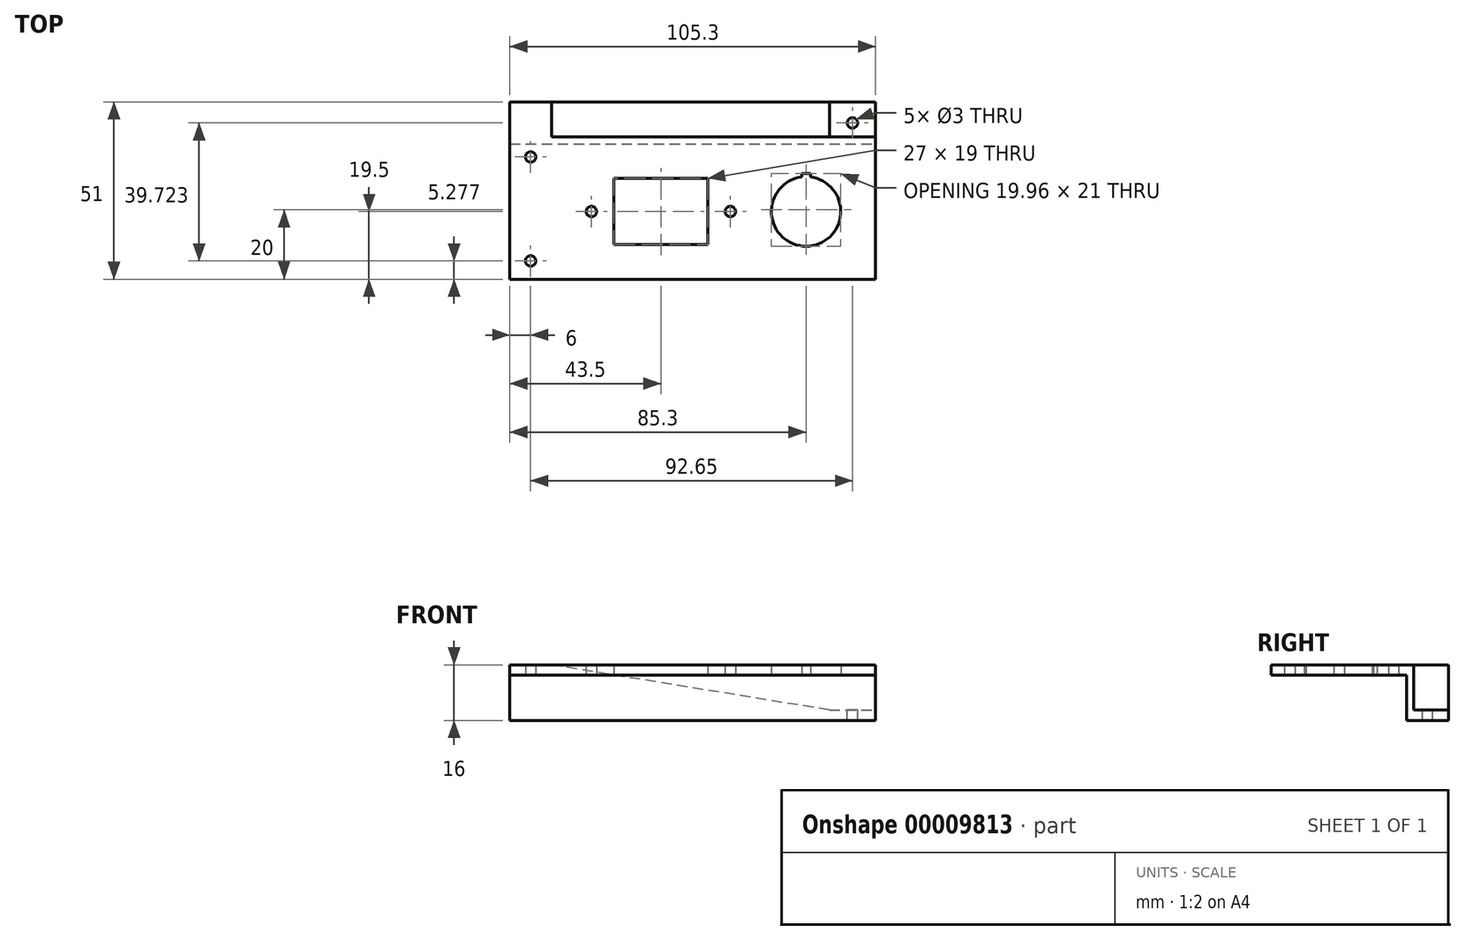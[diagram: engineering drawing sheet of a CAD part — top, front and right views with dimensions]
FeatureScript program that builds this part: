
annotation { "Feature Type Name" : "Feature", "Feature Type Description" : "" }
export const myFeature = defineFeature(function(context is Context, id is Id, definition is map)
    precondition{}
    {
        {
            var Q0;
            Q0=qCreatedBy(makeId("Top.planeOp"),FACE);
            var sketch = newSketch(context, id + "F0", { "sketchPlane" : qUnion([Q0])});
            skLineSegment(sketch, "E0.bottom", {"start": v(-13.5, 9.5) * mm, "end": v(13.5, 9.5) * mm});
            skLineSegment(sketch, "E0.top", {"start": v(-13.5, -9.5) * mm, "end": v(13.5, -9.5) * mm});
            skLineSegment(sketch, "E0.left", {"start": v(-13.5, 9.5) * mm, "end": v(-13.5, -9.5) * mm});
            skLineSegment(sketch, "E0.right", {"start": v(13.5, 9.5) * mm, "end": v(13.5, -9.5) * mm});
            skCircle(sketch, "E1", {"center": v(-20, 0) * mm, "radius": 1.5 * mm});
            skCircle(sketch, "E2.0.MirrorC", {"center": v(20, 0) * mm, "radius": 1.5 * mm});
            skCircle(sketch, "E3", {"center": v(41.8, 0) * mm, "radius": 10 * mm});
            skLineSegment(sketch, "E4", {"start": v(40.55, 9.92) * mm, "end": v(40.55, 11) * mm});
            skLineSegment(sketch, "E5", {"start": v(40.55, 11) * mm, "end": v(43.05, 11) * mm});
            skLineSegment(sketch, "E6", {"start": v(43.05, 11) * mm, "end": v(43.05, 9.92) * mm});
            skLineSegment(sketch, "E7.bottom", {"start": v(-43.5, 31.5) * mm, "end": v(61.8, 31.5) * mm});
            skLineSegment(sketch, "E7.top", {"start": v(-43.5, -19.5) * mm, "end": v(61.8, -19.5) * mm});
            skLineSegment(sketch, "E7.left", {"start": v(-43.5, 31.5) * mm, "end": v(-43.5, -19.5) * mm});
            skLineSegment(sketch, "E7.right", {"start": v(61.8, 31.5) * mm, "end": v(61.8, -19.5) * mm});
            skCircle(sketch, "E8", {"center": v(-37.5, -14.22) * mm, "radius": 1.5 * mm});
            skCircle(sketch, "E9", {"center": v(-37.5, 15.7) * mm, "radius": 1.5 * mm});
            skSolve(sketch);
        }
        {
            var Q0;
            Q0=makeQuery(id+"F0.imprint","IMPRINT",FACE,{"disambiguationData":[TD([[makeQuery(id+"F0.imprint","IMPRINT",EDGE,{"derivedFrom":sQuery(id+"F0.wireOp",EDGE,"E0.bottom")}),1.0]])]});
            extrude(context, id + "F1", {"entities" : qUnion([Q0]), "depth" : 3 * mm});
        }
        {
            var Q0;
            Q0=makeQuery(id+"F1.opExtrude","CAP_FACE",FACE,{"disambiguationData":[OSD([sQuery(id+"F0.wireOp",EDGE,"E0.bottom"),sQuery(id+"F0.wireOp",EDGE,"E0.top"),sQuery(id+"F0.wireOp",EDGE,"E0.left"),sQuery(id+"F0.wireOp",EDGE,"E0.right"),sQuery(id+"F0.wireOp",EDGE,"E1"),sQuery(id+"F0.wireOp",EDGE,"E2.0.MirrorC"),sQuery(id+"F0.wireOp",EDGE,"E3"),sQuery(id+"F0.wireOp",EDGE,"E4"),sQuery(id+"F0.wireOp",EDGE,"E5"),sQuery(id+"F0.wireOp",EDGE,"E6"),sQuery(id+"F0.wireOp",EDGE,"E7.bottom"),sQuery(id+"F0.wireOp",EDGE,"E7.top"),sQuery(id+"F0.wireOp",EDGE,"E7.left"),sQuery(id+"F0.wireOp",EDGE,"E7.right")])],"isStart":true});
            var sketch = newSketch(context, id + "F2", { "sketchPlane" : qUnion([Q0])});
            skLineSegment(sketch, "E10.bottom", {"start": v(-43.5, -31.5) * mm, "end": v(61.8, -31.5) * mm});
            skLineSegment(sketch, "E10.top", {"start": v(-43.5, -19.5) * mm, "end": v(61.8, -19.5) * mm});
            skLineSegment(sketch, "E10.left", {"start": v(-43.5, -31.5) * mm, "end": v(-43.5, -19.5) * mm});
            skLineSegment(sketch, "E10.right", {"start": v(61.8, -31.5) * mm, "end": v(61.8, -19.5) * mm});
            skSolve(sketch);
        }
        {
            var Q0;
            Q0=makeQuery(id+"F2.imprint","IMPRINT",FACE,{"disambiguationData":[TD([[makeQuery(id+"F2.imprint","IMPRINT",EDGE,{"derivedFrom":sQuery(id+"F2.wireOp",EDGE,"E10.bottom")}),1.0]])]});
            extrude(context, id + "F3", {"entities" : qUnion([Q0]), "operationType" : NewBodyOperationType.ADD, "depth" : 13 * mm});
        }
        {
            var Q0;
            Q0=makeQuery(id+"F1.opExtrude","CAP_FACE",FACE,{"disambiguationData":[OSD([sQuery(id+"F0.wireOp",EDGE,"E0.bottom"),sQuery(id+"F0.wireOp",EDGE,"E0.top"),sQuery(id+"F0.wireOp",EDGE,"E0.left"),sQuery(id+"F0.wireOp",EDGE,"E0.right"),sQuery(id+"F0.wireOp",EDGE,"E1"),sQuery(id+"F0.wireOp",EDGE,"E2.0.MirrorC"),sQuery(id+"F0.wireOp",EDGE,"E3"),sQuery(id+"F0.wireOp",EDGE,"E4"),sQuery(id+"F0.wireOp",EDGE,"E5"),sQuery(id+"F0.wireOp",EDGE,"E6"),sQuery(id+"F0.wireOp",EDGE,"E7.bottom"),sQuery(id+"F0.wireOp",EDGE,"E7.top"),sQuery(id+"F0.wireOp",EDGE,"E7.left"),sQuery(id+"F0.wireOp",EDGE,"E7.right")])],"isStart":false});
            var sketch = newSketch(context, id + "F4", { "sketchPlane" : qUnion([Q0])});
            skLineSegment(sketch, "E11.top", {"start": v(-31.5, 21.5) * mm, "end": v(61.8, 21.5) * mm});
            skLineSegment(sketch, "E11.right", {"start": v(61.8, 31.5) * mm, "end": v(61.8, 21.5) * mm});
            skLineSegment(sketch, "E12", {"start": v(-31.5, 21.5) * mm, "end": v(-31.5, 31.5) * mm});
            skLineSegment(sketch, "E13", {"start": v(-31.5, 31.5) * mm, "end": v(61.8, 31.5) * mm});
            skSolve(sketch);
        }
        {
            var Q0;
            Q0 = qSketchRegion(id + "F4", true);
            extrude(context, id + "F5", {"entities" : qUnion([Q0]), "operationType" : NewBodyOperationType.REMOVE, "oppositeDirection" : true, "depth" : 13 * mm});
        }
        {
            var Q0;
            Q0=makeQuery(id+"F5.boolean.opBoolean","COPY",EDGE,{"derivedFrom":makeQuery(id+"F5.opExtrude","CAP_EDGE",EDGE,{"disambiguationData":[OSD([sQuery(id+"F4.wireOp",EDGE,"E12")])],"isStart":false})});
            chamfer(context, id + "F6", {"entities" : qUnion([Q0]), "chamferType" : ChamferType.TWO_OFFSETS, "width1" : 13 * mm, "oppositeDirection" : false, "width2" : 80 * mm, "tangentPropagation" : true});
        }
        {
            var Q0;
            Q0=makeQuery(id+"F5.boolean.opBoolean","COPY",FACE,{"derivedFrom":makeQuery(id+"F5.opExtrude","CAP_FACE",FACE,{"disambiguationData":[OSD([sQuery(id+"F4.wireOp",EDGE,"E11.top"),sQuery(id+"F4.wireOp",EDGE,"E11.right"),sQuery(id+"F4.wireOp",EDGE,"E12"),sQuery(id+"F4.wireOp",EDGE,"E13")])],"isStart":false})});
            var sketch = newSketch(context, id + "F7", { "sketchPlane" : qUnion([Q0])});
            skCircle(sketch, "E14", {"center": v(55.15, 25.5) * mm, "radius": 1.5 * mm});
            skSolve(sketch);
        }
        {
            var Q0;
            Q0=makeQuery(id+"F7.imprint","IMPRINT",FACE,{"disambiguationData":[TD([[makeQuery(id+"F7.imprint","IMPRINT",EDGE,{"derivedFrom":sQuery(id+"F7.wireOp",EDGE,"E14")}),1.0]])]});
            extrude(context, id + "F8", {"entities" : qUnion([Q0]), "operationType" : NewBodyOperationType.REMOVE, "oppositeDirection" : true, "depth" : 25 * mm});
        }
    });
